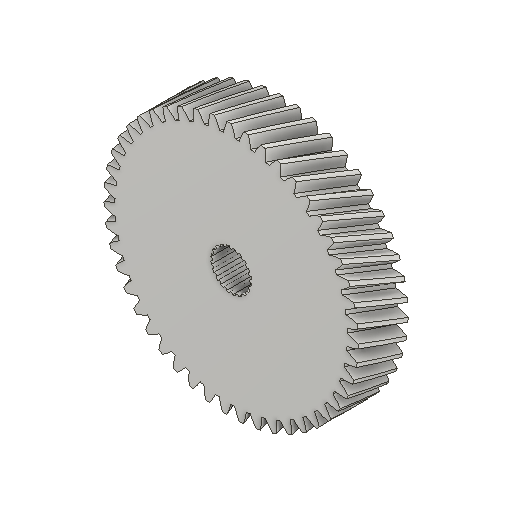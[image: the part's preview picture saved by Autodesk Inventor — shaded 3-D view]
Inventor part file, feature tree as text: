
AUTODESK INVENTOR PART (.ipt)
format: ipt  version: 2025.1 (Build 291241020, 241B)  size: 762,880 bytes
history: native  units: mm (DEFAULTED — no unit token found)
features: plane x3, other x3, extrude x2, sketch x2
ambient origin geometry x8: Origin, YZ Plane, XZ Plane, XY Plane, X Axis, Y Axis, Z Axis, Center Point
bodies: Solid1 (feature_tree)
feature tree (10):
  extrude  "Extrusion1"  Depth=15.0mm TaperAngle=0.0deg
  plane  "Work Plane2"
  plane  "Work Plane8"
  plane  "Work Plane9"
  other  "Spur Gear"
  extrude  "Extrusion2"  Depth=10.0mm TaperAngle=0.0deg
  sketch  "Sketch1"  dims[d0=76.609237mm d1=15.0mm d2=0.0mm]
  other  "Srf1"
  sketch  "Sketch Circular Pattern1"  dims[d3=73.553464mm d4=10.0mm d5=0.0mm d16=63.909111mm d17=0.0mm d34=0.668424mm d39=0.0mm d41=0.0mm d43=63.909111mm d46=63.909111mm d47=0.0mm d48=0.0mm d49=12.217mm d50=0.0mm d51=0.0mm d52=6.1135mm d53=0.515mm d54=200.0mm d56=360.0deg]
  other  "Pitch Diameter"
